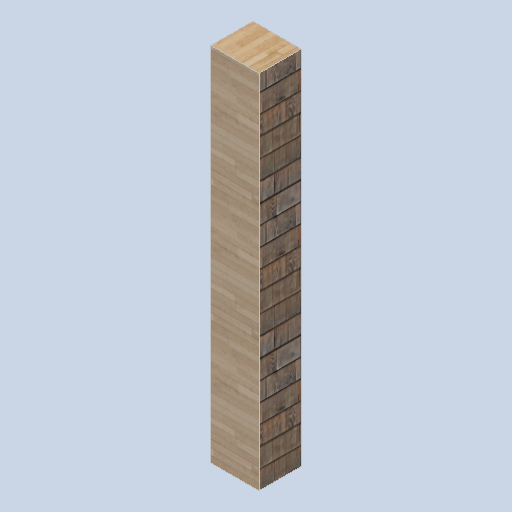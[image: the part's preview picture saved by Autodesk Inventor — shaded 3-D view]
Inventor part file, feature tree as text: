
AUTODESK INVENTOR PART (.ipt)
format: ipt  version: 2024.2 (Build 282272000, 272)  size: 174,080 bytes
history: native  units: in
note: dims shown in document units (in); Inventor stores cm internally (conversion verified against a paired STEP export)
features: other x3, sketch x1
ambient origin geometry x8: Origin, YZ Plane, XZ Plane, XY Plane, X Axis, Y Axis, Z Axis, Center Point
bodies: Solid1 (feature_tree)
feature tree (4):
  other  "support_column_02.ipt"
  other  "Solid1::support_column_02.ipt"
  other  "TaggingFeature1"
  sketch  "Sketch1"  dims[d0=0.3937in]
